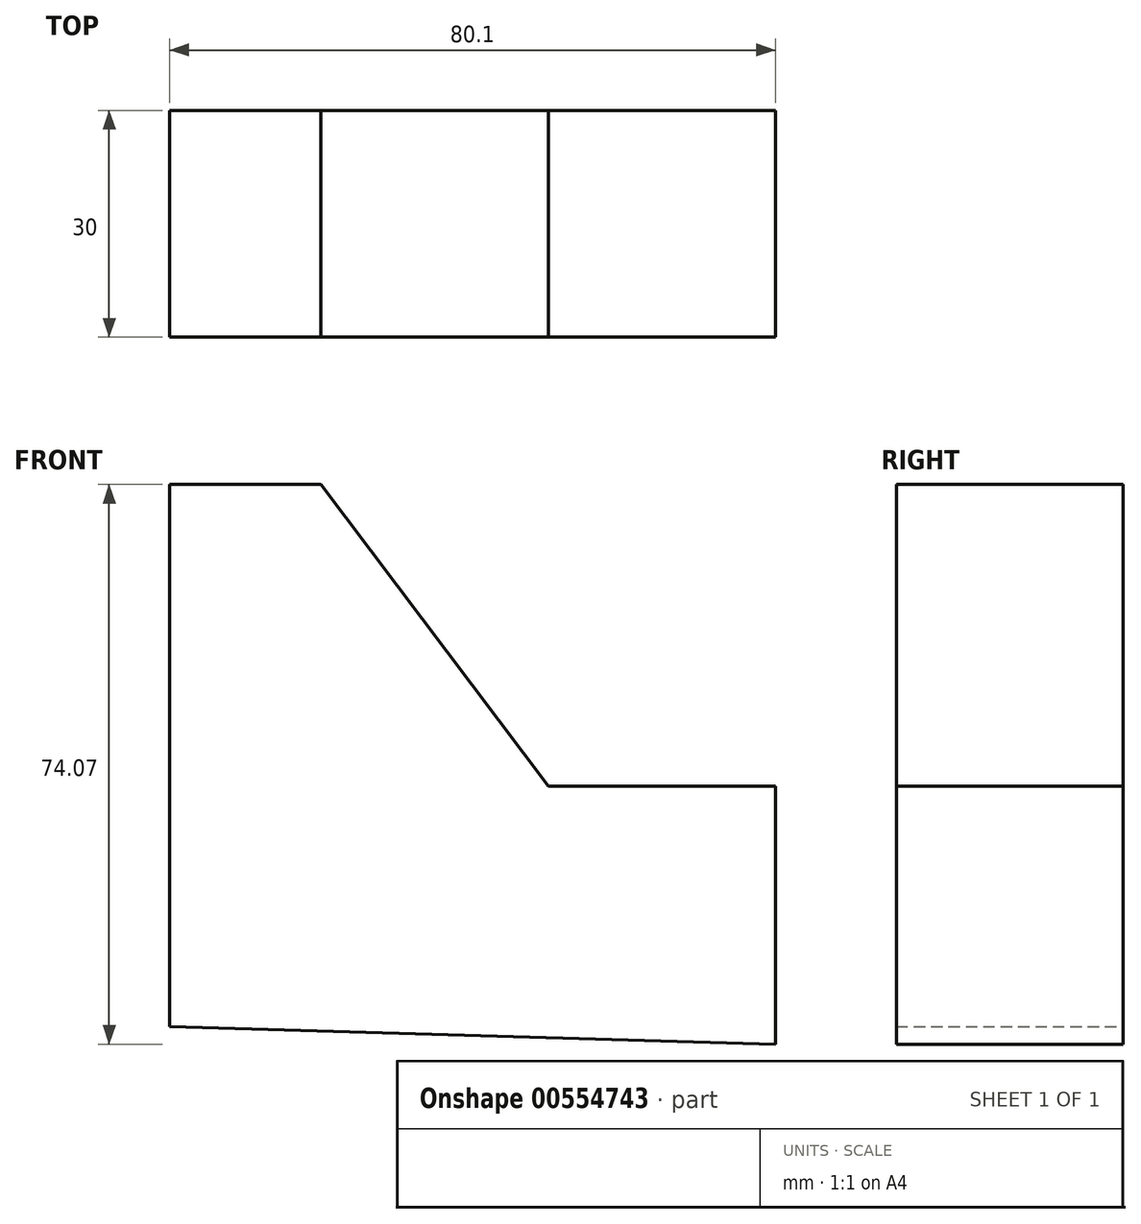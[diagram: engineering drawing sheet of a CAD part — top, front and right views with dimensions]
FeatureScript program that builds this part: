
annotation { "Feature Type Name" : "Feature", "Feature Type Description" : "" }
export const myFeature = defineFeature(function(context is Context, id is Id, definition is map)
    precondition{}
    {
        {
            var Q0;
            Q0=qCreatedBy(makeId("Front.planeOp"),FACE);
            var sketch = newSketch(context, id + "F0", { "sketchPlane" : qUnion([Q0])});
            skLineSegment(sketch, "E0", {"start": v(-63.23, 36.33) * mm, "end": v(-43.23, 36.33) * mm});
            skLineSegment(sketch, "E1", {"start": v(-43.23, 36.33) * mm, "end": v(-13.13, -3.6) * mm});
            skLineSegment(sketch, "E2", {"start": v(-13.13, -3.6) * mm, "end": v(16.87, -3.6) * mm});
            skLineSegment(sketch, "E3", {"start": v(16.87, -3.6) * mm, "end": v(16.87, -37.74) * mm});
            skLineSegment(sketch, "E4", {"start": v(16.87, -37.74) * mm, "end": v(-63.23, -35.39) * mm});
            skLineSegment(sketch, "E5", {"start": v(-63.23, -35.39) * mm, "end": v(-63.23, 36.33) * mm});
            skSolve(sketch);
        }
        {
            var Q0;
            Q0 = qSketchRegion(id + "F0", true);
            var Q1;
            Q1=makeQuery(id+"F0.imprint","IMPRINT",FACE,{"disambiguationData":[TD([[makeQuery(id+"F0.imprint","IMPRINT",EDGE,{"derivedFrom":sQuery(id+"F0.wireOp",EDGE,"E0")}),-1.0]])]});
            extrude(context, id + "F1", {"entities" : qUnion([Q0, Q1]), "depth" : 30 * mm, "offsetDistance" : 25 * mm});
        }
    });
